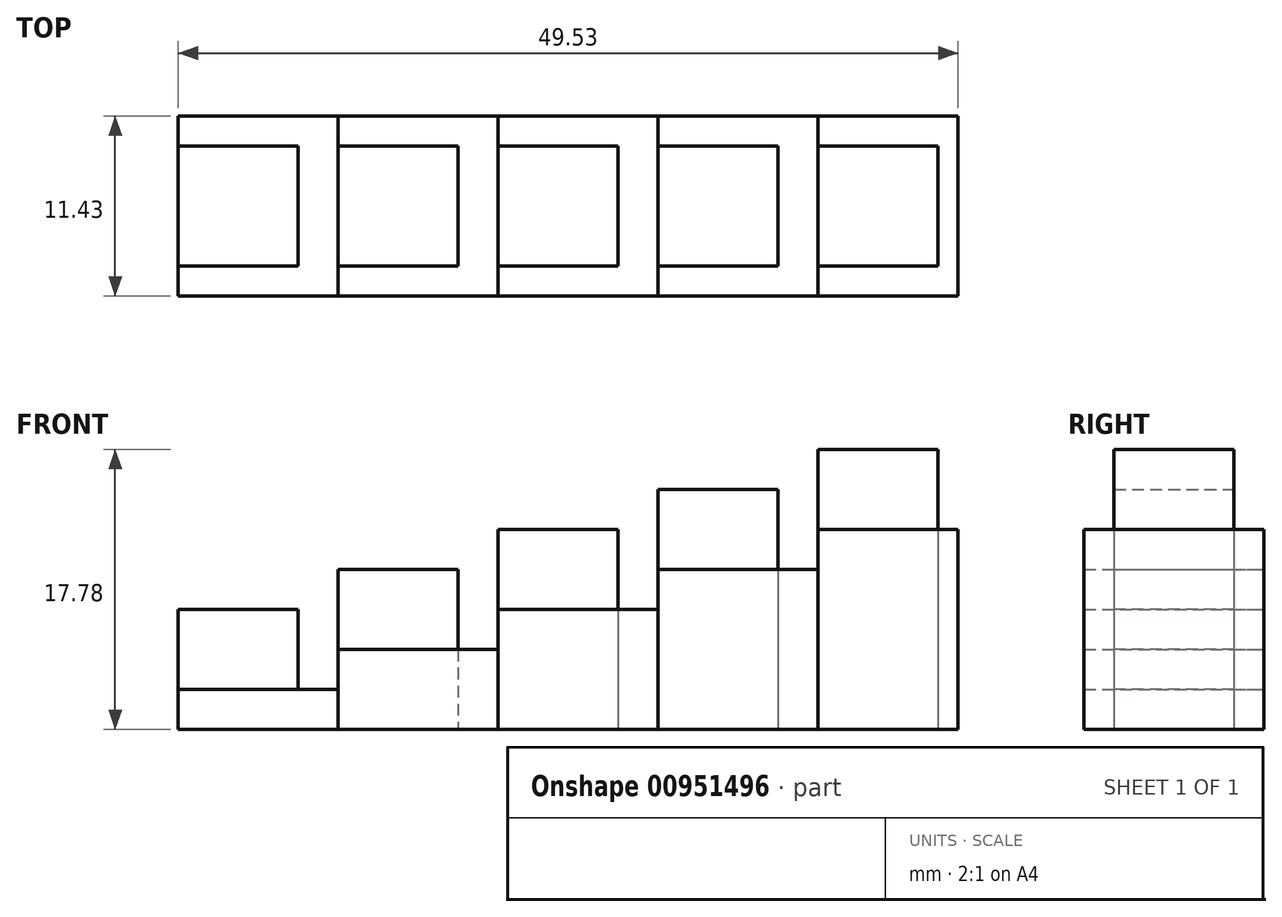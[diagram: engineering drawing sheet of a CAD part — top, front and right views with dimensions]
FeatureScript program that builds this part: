
annotation { "Feature Type Name" : "Feature", "Feature Type Description" : "" }
export const myFeature = defineFeature(function(context is Context, id is Id, definition is map)
    precondition{}
    {
        {
            var Q0;
            Q0=qCreatedBy(makeId("Top.planeOp"),FACE);
            var sketch = newSketch(context, id + "F0", { "sketchPlane" : qUnion([Q0])});
            skLineSegment(sketch, "E0.bottom", {"start": v(-15.3, 8.27) * mm, "end": v(-24.18, 8.27) * mm});
            skLineSegment(sketch, "E0.top", {"start": v(-15.3, 19.7) * mm, "end": v(-24.18, 19.7) * mm});
            skLineSegment(sketch, "E0.left", {"start": v(-15.3, 8.27) * mm, "end": v(-15.3, 19.7) * mm});
            skLineSegment(sketch, "E0.right", {"start": v(-24.18, 8.27) * mm, "end": v(-24.18, 19.7) * mm});
            skLineSegment(sketch, "E1.bottom", {"start": v(-24.18, 17.8) * mm, "end": v(-16.56, 17.8) * mm});
            skLineSegment(sketch, "E1.top", {"start": v(-24.18, 10.18) * mm, "end": v(-16.56, 10.18) * mm});
            skLineSegment(sketch, "E1.left", {"start": v(-24.18, 17.8) * mm, "end": v(-24.18, 10.18) * mm});
            skLineSegment(sketch, "E1.right", {"start": v(-16.56, 17.8) * mm, "end": v(-16.56, 10.18) * mm});
            skPoint(sketch, "E2", {"position": v(-24.18, 13.99) * mm});
            skLineSegment(sketch, "E3.bottom", {"start": v(-24.18, 8.27) * mm, "end": v(-34.34, 8.27) * mm});
            skLineSegment(sketch, "E3.top", {"start": v(-24.18, 19.7) * mm, "end": v(-34.34, 19.7) * mm});
            skLineSegment(sketch, "E3.right", {"start": v(-34.34, 8.27) * mm, "end": v(-34.34, 19.7) * mm});
            skLineSegment(sketch, "E4.bottom", {"start": v(-34.34, 17.8) * mm, "end": v(-26.72, 17.8) * mm});
            skLineSegment(sketch, "E4.top", {"start": v(-34.34, 10.18) * mm, "end": v(-26.72, 10.18) * mm});
            skLineSegment(sketch, "E4.left", {"start": v(-34.34, 17.8) * mm, "end": v(-34.34, 10.18) * mm});
            skLineSegment(sketch, "E4.right", {"start": v(-26.72, 17.8) * mm, "end": v(-26.72, 10.18) * mm});
            skPoint(sketch, "E5", {"position": v(-34.34, 13.99) * mm});
            skLineSegment(sketch, "E6.bottom", {"start": v(-34.34, 8.27) * mm, "end": v(-44.5, 8.27) * mm});
            skLineSegment(sketch, "E6.top", {"start": v(-34.34, 19.7) * mm, "end": v(-44.5, 19.7) * mm});
            skLineSegment(sketch, "E6.right", {"start": v(-44.5, 8.27) * mm, "end": v(-44.5, 19.7) * mm});
            skLineSegment(sketch, "E7.bottom", {"start": v(-44.5, 17.8) * mm, "end": v(-36.88, 17.8) * mm});
            skLineSegment(sketch, "E7.top", {"start": v(-44.5, 10.18) * mm, "end": v(-36.88, 10.18) * mm});
            skLineSegment(sketch, "E7.left", {"start": v(-44.5, 17.8) * mm, "end": v(-44.5, 10.18) * mm});
            skLineSegment(sketch, "E7.right", {"start": v(-36.88, 17.8) * mm, "end": v(-36.88, 10.18) * mm});
            skPoint(sketch, "E8", {"position": v(-44.5, 13.99) * mm});
            skLineSegment(sketch, "E9.bottom", {"start": v(-44.5, 8.27) * mm, "end": v(-54.66, 8.27) * mm});
            skLineSegment(sketch, "E9.top", {"start": v(-44.5, 19.7) * mm, "end": v(-54.66, 19.7) * mm});
            skLineSegment(sketch, "E9.right", {"start": v(-54.66, 8.27) * mm, "end": v(-54.66, 19.7) * mm});
            skLineSegment(sketch, "E10.bottom", {"start": v(-54.66, 17.8) * mm, "end": v(-47.04, 17.8) * mm});
            skLineSegment(sketch, "E10.top", {"start": v(-54.66, 10.18) * mm, "end": v(-47.04, 10.18) * mm});
            skLineSegment(sketch, "E10.left", {"start": v(-54.66, 17.8) * mm, "end": v(-54.66, 10.18) * mm});
            skLineSegment(sketch, "E10.right", {"start": v(-47.04, 17.8) * mm, "end": v(-47.04, 10.18) * mm});
            skPoint(sketch, "E11", {"position": v(-54.66, 13.99) * mm});
            skLineSegment(sketch, "E12.bottom", {"start": v(-54.66, 8.27) * mm, "end": v(-64.82, 8.27) * mm});
            skLineSegment(sketch, "E12.top", {"start": v(-54.66, 19.7) * mm, "end": v(-64.82, 19.7) * mm});
            skLineSegment(sketch, "E12.right", {"start": v(-64.82, 8.27) * mm, "end": v(-64.82, 19.7) * mm});
            skLineSegment(sketch, "E13.bottom", {"start": v(-64.82, 17.8) * mm, "end": v(-57.2, 17.8) * mm});
            skLineSegment(sketch, "E13.top", {"start": v(-64.82, 10.18) * mm, "end": v(-57.2, 10.18) * mm});
            skLineSegment(sketch, "E13.left", {"start": v(-64.82, 17.8) * mm, "end": v(-64.82, 10.18) * mm});
            skLineSegment(sketch, "E13.right", {"start": v(-57.2, 17.8) * mm, "end": v(-57.2, 10.18) * mm});
            skPoint(sketch, "E14", {"position": v(-64.82, 13.99) * mm});
            skSolve(sketch);
        }
        {
            var Q0;
            Q0=makeQuery(id+"F0.imprint","IMPRINT",FACE,{"disambiguationData":[TD([[makeQuery(id+"F0.imprint","IMPRINT",EDGE,{"derivedFrom":sQuery(id+"F0.wireOp",EDGE,"E13.bottom")}),-1.0]])]});
            extrude(context, id + "F1", {"entities" : qUnion([Q0]), "depth" : 7.62 * mm, "offsetDistance" : 25.4 * mm});
        }
        {
            var Q0;
            Q0=makeQuery(id+"F0.imprint","IMPRINT",FACE,{"disambiguationData":[TD([[makeQuery(id+"F0.imprint","IMPRINT",EDGE,{"derivedFrom":sQuery(id+"F0.wireOp",EDGE,"E12.bottom")}),-1.0]])]});
            extrude(context, id + "F2", {"entities" : qUnion([Q0]), "operationType" : NewBodyOperationType.ADD, "depth" : 2.54 * mm, "offsetDistance" : 25.4 * mm});
        }
        {
            var Q0;
            Q0=makeQuery(id+"F0.imprint","IMPRINT",FACE,{"disambiguationData":[TD([[makeQuery(id+"F0.imprint","IMPRINT",EDGE,{"derivedFrom":sQuery(id+"F0.wireOp",EDGE,"E10.bottom")}),-1.0]])]});
            extrude(context, id + "F3", {"entities" : qUnion([Q0]), "depth" : 10.16 * mm, "offsetDistance" : 25.4 * mm});
        }
        {
            var Q0;
            Q0=makeQuery(id+"F0.imprint","IMPRINT",FACE,{"disambiguationData":[TD([[makeQuery(id+"F0.imprint","IMPRINT",EDGE,{"derivedFrom":sQuery(id+"F0.wireOp",EDGE,"E9.bottom")}),-1.0]])]});
            extrude(context, id + "F4", {"entities" : qUnion([Q0]), "depth" : 5.08 * mm, "offsetDistance" : 25.4 * mm});
        }
        {
            var Q0;
            Q0=makeQuery(id+"F0.imprint","IMPRINT",FACE,{"disambiguationData":[TD([[makeQuery(id+"F0.imprint","IMPRINT",EDGE,{"derivedFrom":sQuery(id+"F0.wireOp",EDGE,"E7.bottom")}),-1.0]])]});
            extrude(context, id + "F5", {"entities" : qUnion([Q0]), "depth" : 12.7 * mm, "offsetDistance" : 25.4 * mm});
        }
        {
            var Q0;
            Q0=makeQuery(id+"F0.imprint","IMPRINT",FACE,{"disambiguationData":[TD([[makeQuery(id+"F0.imprint","IMPRINT",EDGE,{"derivedFrom":sQuery(id+"F0.wireOp",EDGE,"E6.bottom")}),-1.0]])]});
            extrude(context, id + "F6", {"entities" : qUnion([Q0]), "depth" : 7.62 * mm, "offsetDistance" : 25.4 * mm});
        }
        {
            var Q0;
            Q0=makeQuery(id+"F0.imprint","IMPRINT",FACE,{"disambiguationData":[TD([[makeQuery(id+"F0.imprint","IMPRINT",EDGE,{"derivedFrom":sQuery(id+"F0.wireOp",EDGE,"E4.bottom")}),-1.0]])]});
            extrude(context, id + "F7", {"entities" : qUnion([Q0]), "depth" : 15.24 * mm, "offsetDistance" : 25.4 * mm});
        }
        {
            var Q0;
            Q0=makeQuery(id+"F0.imprint","IMPRINT",FACE,{"disambiguationData":[TD([[makeQuery(id+"F0.imprint","IMPRINT",EDGE,{"derivedFrom":sQuery(id+"F0.wireOp",EDGE,"E3.bottom")}),-1.0]])]});
            extrude(context, id + "F8", {"entities" : qUnion([Q0]), "depth" : 10.16 * mm, "offsetDistance" : 25.4 * mm});
        }
        {
            var Q0;
            Q0=makeQuery(id+"F0.imprint","IMPRINT",FACE,{"disambiguationData":[TD([[makeQuery(id+"F0.imprint","IMPRINT",EDGE,{"derivedFrom":sQuery(id+"F0.wireOp",EDGE,"E1.bottom")}),-1.0]])]});
            extrude(context, id + "F9", {"entities" : qUnion([Q0]), "depth" : 17.78 * mm, "offsetDistance" : 25.4 * mm});
        }
        {
            var Q0;
            Q0=makeQuery(id+"F0.imprint","IMPRINT",FACE,{"disambiguationData":[TD([[makeQuery(id+"F0.imprint","IMPRINT",EDGE,{"derivedFrom":sQuery(id+"F0.wireOp",EDGE,"E0.bottom")}),-1.0]])]});
            extrude(context, id + "F10", {"entities" : qUnion([Q0]), "depth" : 12.7 * mm, "offsetDistance" : 25.4 * mm});
        }
    });
